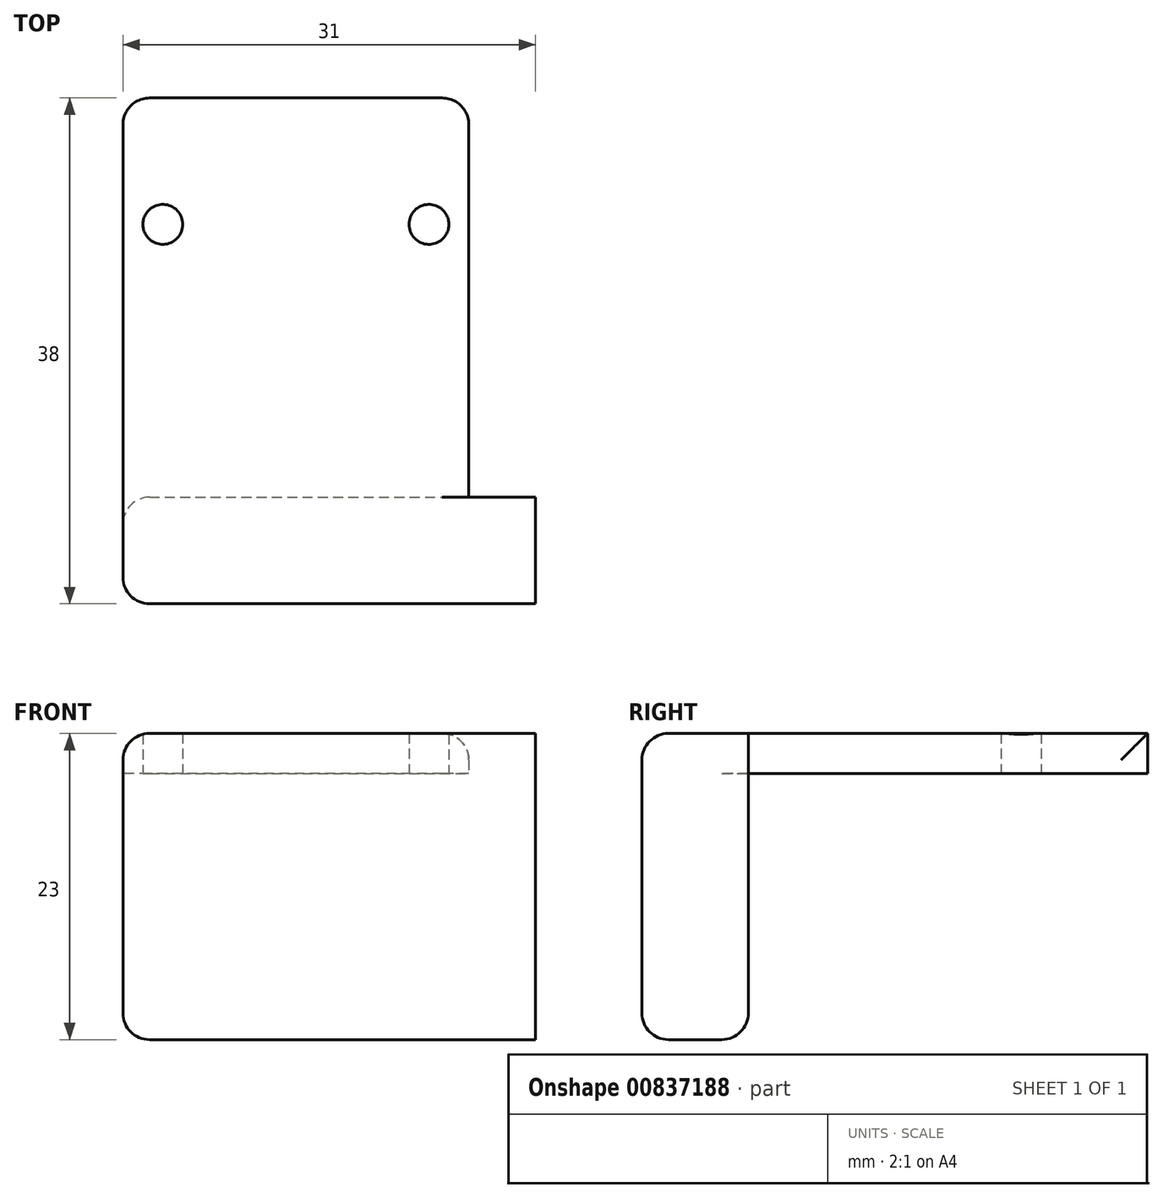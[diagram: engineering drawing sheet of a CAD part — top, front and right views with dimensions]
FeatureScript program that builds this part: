
annotation { "Feature Type Name" : "Feature", "Feature Type Description" : "" }
export const myFeature = defineFeature(function(context is Context, id is Id, definition is map)
    precondition{}
    {
        {
            var Q0;
            Q0=qCreatedBy(makeId("Top.planeOp"),FACE);
            var sketch = newSketch(context, id + "F0", { "sketchPlane" : qUnion([Q0])});
            skLineSegment(sketch, "E0.bottom", {"start": v(13, -19) * mm, "end": v(-13, -19) * mm});
            skLineSegment(sketch, "E0.top", {"start": v(13, 19) * mm, "end": v(-13, 19) * mm});
            skLineSegment(sketch, "E0.left", {"start": v(13, -19) * mm, "end": v(13, 19) * mm});
            skLineSegment(sketch, "E0.right", {"start": v(-13, -19) * mm, "end": v(-13, 19) * mm});
            skPoint(sketch, "E0.middle", {"position": v(0, 0) * mm});
            skCircle(sketch, "E1", {"center": v(-10, 9.5) * mm, "radius": 1.5 * mm});
            skCircle(sketch, "E2", {"center": v(10, 9.5) * mm, "radius": 1.5 * mm});
            skSolve(sketch);
        }
        {
            var Q0;
            Q0=makeQuery(id+"F0.imprint","IMPRINT",FACE,{"disambiguationData":[TD([[makeQuery(id+"F0.imprint","IMPRINT",EDGE,{"derivedFrom":sQuery(id+"F0.wireOp",EDGE,"E0.bottom")}),-1.0]])]});
            extrude(context, id + "F1", {"entities" : qUnion([Q0]), "depth" : 3 * mm, "offsetDistance" : 25 * mm});
        }
        {
            var Q0;
            Q0=makeQuery(id+"F1.opExtrude","CAP_FACE",FACE,{"disambiguationData":[OSD([sQuery(id+"F0.wireOp",EDGE,"E0.bottom"),sQuery(id+"F0.wireOp",EDGE,"E0.top"),sQuery(id+"F0.wireOp",EDGE,"E0.left"),sQuery(id+"F0.wireOp",EDGE,"E0.right"),sQuery(id+"F0.wireOp",EDGE,"E1"),sQuery(id+"F0.wireOp",EDGE,"E2")])],"isStart":true});
            var sketch = newSketch(context, id + "F2", { "sketchPlane" : qUnion([Q0])});
            skLineSegment(sketch, "E3", {"start": v(-13, 11) * mm, "end": v(13, 11) * mm});
            skSolve(sketch);
        }
        {
            var Q0;
            {var subQ0=sQuery(id+"F2.wireOp",EDGE,"E3");Q0=makeQuery(id+"F2.imprint","IMPRINT",FACE,{"disambiguationData":[TD([[makeQuery(id+"F2.imprint","IMPRINT",EDGE,{"derivedFrom":subQ0}),1.0]])]});}
            extrude(context, id + "F3", {"entities" : qUnion([Q0]), "operationType" : NewBodyOperationType.ADD, "depth" : 20 * mm, "offsetDistance" : 25 * mm});
        }
        {
            var Q0;
            {var subQ0=sQuery(id+"F0.wireOp",EDGE,"E0.left");Q0=makeQuery(id+"F3.boolean.opBoolean","MERGE",FACE,{"derivedFrom":[makeQuery(id+"F1.opExtrude","SWEPT_FACE",FACE,{"disambiguationData":[OSD([subQ0])]}),makeQuery(id+"F3.opExtrude","SWEPT_FACE",FACE,{"disambiguationData":[OSD([subQ0])]})]});}
            var sketch = newSketch(context, id + "F4", { "sketchPlane" : qUnion([Q0])});
            skLineSegment(sketch, "E4", {"start": v(-11, 0) * mm, "end": v(-11, 3) * mm});
            skSolve(sketch);
        }
        {
            var Q0;
            {var subQ3=sQuery(id+"F4.wireOp",EDGE,"E4");Q0=makeQuery(id+"F4.imprint","IMPRINT",FACE,{"disambiguationData":[TD([[makeQuery(id+"F4.imprint","IMPRINT",EDGE,{"derivedFrom":subQ3}),1.0]])]});}
            extrude(context, id + "F5", {"entities" : qUnion([Q0]), "operationType" : NewBodyOperationType.ADD, "depth" : 5 * mm, "offsetDistance" : 25 * mm});
        }
        {
            var Q0;
            Q0=makeQuery(id+"F5.opExtrude","CAP_EDGE",EDGE,{"disambiguationData":[OSD([sQuery(id+"F0.wireOp",EDGE,"E0.left"),sQuery(id+"F2.wireOp",EDGE,"E3"),sQuery(id+"F4.wireOp",EDGE,"E4")])],"isStart":true});
            var Q1;
            Q1=makeQuery(id+"F3.opExtrude","SWEPT_EDGE",EDGE,{"disambiguationData":[OSD([sQuery(id+"F0.wireOp",EDGE,"E0.right"),sQuery(id+"F2.wireOp",EDGE,"E3")])]});
            var Q2;
            {var subQ0=sQuery(id+"F0.wireOp",EDGE,"E0.right");var subQ1=sQuery(id+"F0.wireOp",EDGE,"E0.bottom");Q2=makeQuery(id+"F3.boolean.opBoolean","MERGE",EDGE,{"derivedFrom":[makeQuery(id+"F1.opExtrude","SWEPT_EDGE",EDGE,{"disambiguationData":[OSD([subQ1,subQ0])]}),makeQuery(id+"F3.opExtrude","SWEPT_EDGE",EDGE,{"disambiguationData":[OSD([subQ1,subQ0])]})]});}
            var Q3;
            Q3=makeQuery(id+"F1.opExtrude","SWEPT_EDGE",EDGE,{"disambiguationData":[OSD([sQuery(id+"F0.wireOp",EDGE,"E0.top"),sQuery(id+"F0.wireOp",EDGE,"E0.left")])]});
            var Q4;
            Q4=makeQuery(id+"F1.opExtrude","SWEPT_EDGE",EDGE,{"disambiguationData":[OSD([sQuery(id+"F0.wireOp",EDGE,"E0.top"),sQuery(id+"F0.wireOp",EDGE,"E0.right")])]});
            var Q5;
            Q5=makeQuery(id+"F1.opExtrude","CAP_EDGE",EDGE,{"disambiguationData":[OSD([sQuery(id+"F0.wireOp",EDGE,"E0.right")])],"isStart":false});
            var Q6;
            Q6=makeQuery(id+"F1.opExtrude","CAP_EDGE",EDGE,{"disambiguationData":[OSD([sQuery(id+"F0.wireOp",EDGE,"E0.left")])],"isStart":false});
            var Q7;
            {var subQ0=sQuery(id+"F2.wireOp",EDGE,"E3");Q7=makeQuery(id+"F5.boolean.opBoolean","MERGE",EDGE,{"derivedFrom":[makeQuery(id+"F3.opExtrude","CAP_EDGE",EDGE,{"disambiguationData":[OSD([subQ0])],"isStart":false}),makeQuery(id+"F5.opExtrude","SWEPT_EDGE",EDGE,{"disambiguationData":[OSD([sQuery(id+"F0.wireOp",EDGE,"E0.left"),subQ0])]})]});}
            var Q8;
            {var subQ0=sQuery(id+"F0.wireOp",EDGE,"E0.left");var subQ1=sQuery(id+"F0.wireOp",EDGE,"E0.bottom");Q8=makeQuery(id+"F5.boolean.opBoolean","MERGE",EDGE,{"derivedFrom":[makeQuery(id+"F3.opExtrude","CAP_EDGE",EDGE,{"disambiguationData":[OSD([subQ1])],"isStart":false}),makeQuery(id+"F5.opExtrude","SWEPT_EDGE",EDGE,{"disambiguationData":[OSD([subQ1,subQ0]),TDD([makeQuery(id+"F4.imprint","INTERSECT",VERTEX,{"derivedFrom":[makeQuery(id+"F3.opExtrude","CAP_EDGE",EDGE,{"disambiguationData":[OSD([subQ0])],"isStart":false}),makeQuery(id+"F3.boolean.opBoolean","MERGE",EDGE,{"derivedFrom":[makeQuery(id+"F1.opExtrude","SWEPT_EDGE",EDGE,{"disambiguationData":[OSD([subQ1,subQ0])]}),makeQuery(id+"F3.opExtrude","SWEPT_EDGE",EDGE,{"disambiguationData":[OSD([subQ1,subQ0])]})]})]})])]})]});}
            var Q9;
            Q9=makeQuery(id+"F3.opExtrude","CAP_EDGE",EDGE,{"disambiguationData":[OSD([sQuery(id+"F0.wireOp",EDGE,"E0.right")])],"isStart":false});
            var Q10;
            {var subQ0=sQuery(id+"F0.wireOp",EDGE,"E0.left");var subQ1=sQuery(id+"F0.wireOp",EDGE,"E0.bottom");Q10=makeQuery(id+"F5.boolean.opBoolean","MERGE",EDGE,{"derivedFrom":[makeQuery(id+"F1.opExtrude","CAP_EDGE",EDGE,{"disambiguationData":[OSD([subQ1])],"isStart":false}),makeQuery(id+"F5.opExtrude","SWEPT_EDGE",EDGE,{"disambiguationData":[OSD([subQ1,subQ0]),TDD([makeQuery(id+"F4.imprint","INTERSECT",VERTEX,{"derivedFrom":[makeQuery(id+"F1.opExtrude","CAP_EDGE",EDGE,{"disambiguationData":[OSD([subQ0])],"isStart":false}),makeQuery(id+"F3.boolean.opBoolean","MERGE",EDGE,{"derivedFrom":[makeQuery(id+"F1.opExtrude","SWEPT_EDGE",EDGE,{"disambiguationData":[OSD([subQ1,subQ0])]}),makeQuery(id+"F3.opExtrude","SWEPT_EDGE",EDGE,{"disambiguationData":[OSD([subQ1,subQ0])]})]})]})])]})]});}
            fillet(context, id + "F6", {"entities" : qUnion([Q0, Q1, Q2, Q3, Q4, Q5, Q6, Q7, Q8, Q9, Q10]), "radius" : 2 * mm, "tangentPropagation" : true, "allowEdgeOverflow" : false});
        }
    });
